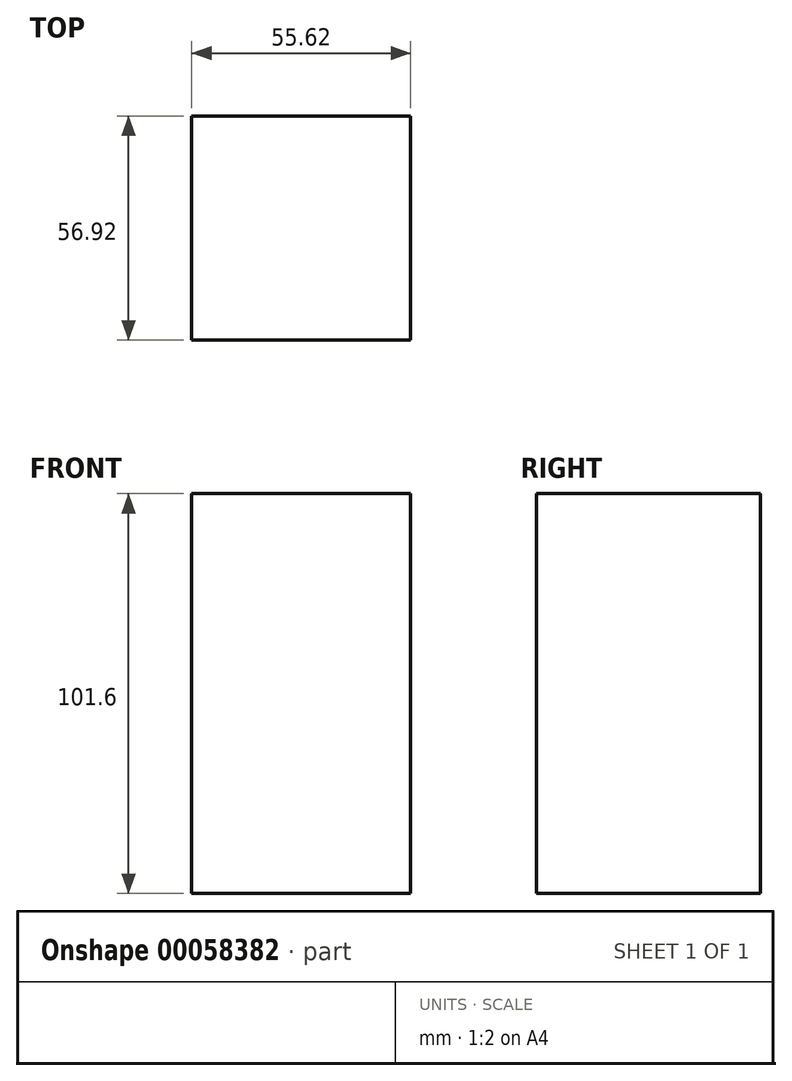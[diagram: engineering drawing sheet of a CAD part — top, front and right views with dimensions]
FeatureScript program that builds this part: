
annotation { "Feature Type Name" : "Feature", "Feature Type Description" : "" }
export const myFeature = defineFeature(function(context is Context, id is Id, definition is map)
    precondition{}
    {
        {
            var Q0;
            Q0=qCreatedBy(makeId("Top.planeOp"),FACE);
            var sketch = newSketch(context, id + "F0", { "sketchPlane" : qUnion([Q0])});
            skLineSegment(sketch, "E0.bottom", {"start": v(0, 0) * mm, "end": v(0, 0) * mm});
            skLineSegment(sketch, "E0.top", {"start": v(0, 0) * mm, "end": v(0, 0) * mm});
            skLineSegment(sketch, "E0.left", {"start": v(0, 0) * mm, "end": v(0, 0) * mm});
            skLineSegment(sketch, "E0.right", {"start": v(0, 0) * mm, "end": v(0, 0) * mm});
            skLineSegment(sketch, "E1.rect.bottom", {"start": v(27.81, 28.46) * mm, "end": v(-27.81, 28.46) * mm});
            skLineSegment(sketch, "E1.rect.top", {"start": v(27.81, -28.46) * mm, "end": v(-27.81, -28.46) * mm});
            skLineSegment(sketch, "E1.rect.left", {"start": v(27.81, 28.46) * mm, "end": v(27.81, -28.46) * mm});
            skLineSegment(sketch, "E1.rect.right", {"start": v(-27.81, 28.46) * mm, "end": v(-27.81, -28.46) * mm});
            skPoint(sketch, "E1.rect.middle", {"position": v(0, 0) * mm});
            skSolve(sketch);
        }
        {
            var Q0;
            Q0=makeQuery(id+"F0.imprint","IMPRINT",FACE,{"disambiguationData":[TD([[makeQuery(id+"F0.imprint","IMPRINT",EDGE,{"derivedFrom":sQuery(id+"F0.wireOp",EDGE,"E1.rect.bottom")}),1.0]])]});
            extrude(context, id + "F1", {"entities" : qUnion([Q0]), "depth" : 101.6 * mm});
        }
    });
